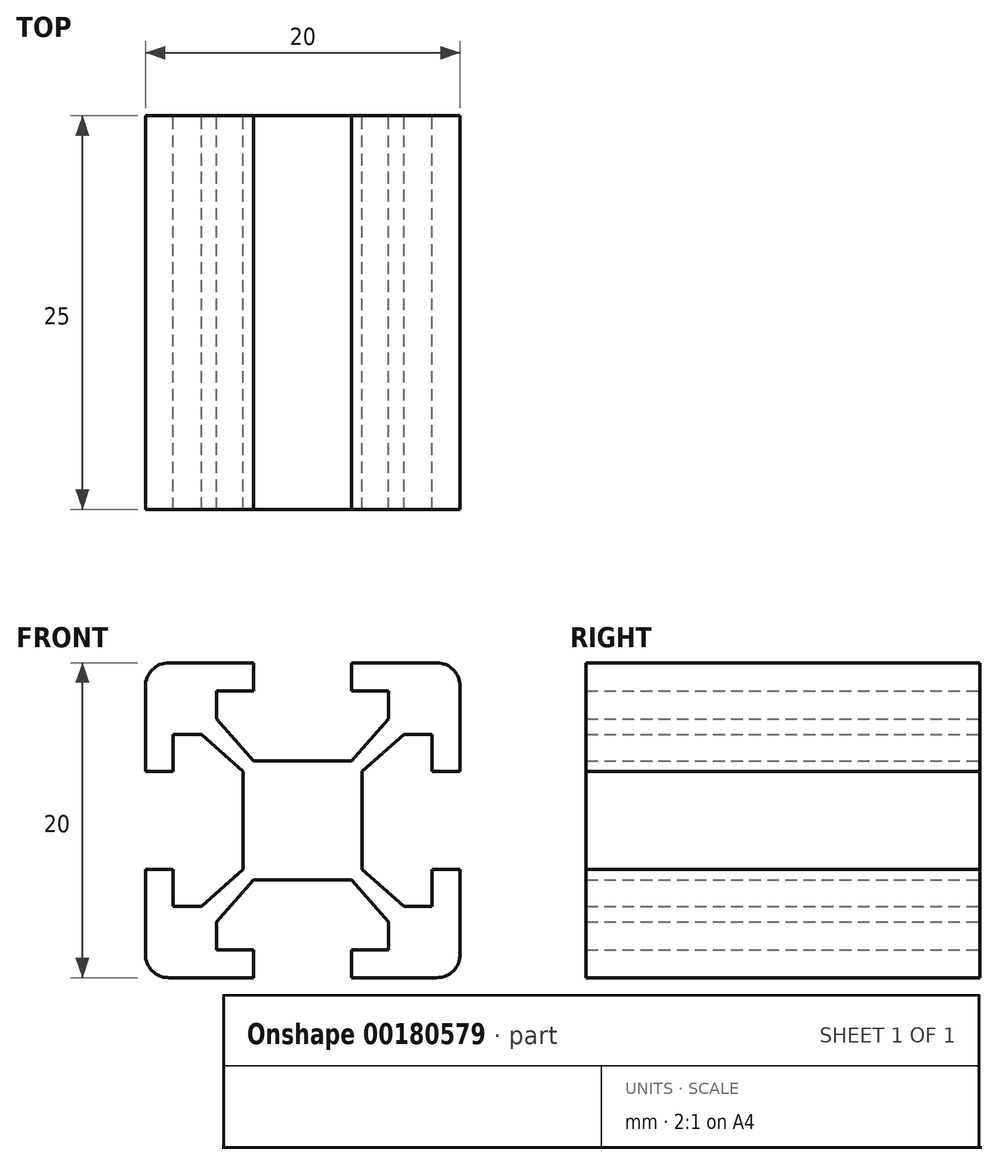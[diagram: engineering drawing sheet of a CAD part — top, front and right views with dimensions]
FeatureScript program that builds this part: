
annotation { "Feature Type Name" : "Feature", "Feature Type Description" : "" }
export const myFeature = defineFeature(function(context is Context, id is Id, definition is map)
    precondition{}
    {
        {
            var Q0;
            Q0=qCreatedBy(makeId("Front.planeOp"),FACE);
            var sketch = newSketch(context, id + "F0", { "sketchPlane" : qUnion([Q0])});
            skLineSegment(sketch, "E0.bottom", {"start": v(10, 10) * mm, "end": v(-10, 10) * mm});
            skLineSegment(sketch, "E0.top", {"start": v(10, -10) * mm, "end": v(-10, -10) * mm});
            skLineSegment(sketch, "E0.left", {"start": v(10, 10) * mm, "end": v(10, -10) * mm});
            skLineSegment(sketch, "E0.right", {"start": v(-10, 10) * mm, "end": v(-10, -10) * mm});
            skPoint(sketch, "E0.middle", {"position": v(0, 0) * mm});
            skLineSegment(sketch, "E1", {"start": v(3.11, 10) * mm, "end": v(3.11, 8.22) * mm});
            skLineSegment(sketch, "E2", {"start": v(3.11, 8.22) * mm, "end": v(5.46, 8.22) * mm});
            skLineSegment(sketch, "E3", {"start": v(5.46, 8.22) * mm, "end": v(5.46, 6.44) * mm});
            skLineSegment(sketch, "E4", {"start": v(5.46, 6.44) * mm, "end": v(3.11, 3.78) * mm});
            skLineSegment(sketch, "E5", {"start": v(3.11, 3.78) * mm, "end": v(0, 3.78) * mm});
            skLineSegment(sketch, "E6.MirrorCS", {"start": v(-3.11, 3.78) * mm, "end": v(0, 3.78) * mm});
            skLineSegment(sketch, "E7.MirrorCS", {"start": v(-5.46, 6.44) * mm, "end": v(-3.11, 3.78) * mm});
            skLineSegment(sketch, "E8.MirrorCS", {"start": v(-3.11, 10) * mm, "end": v(-3.11, 8.22) * mm});
            skLineSegment(sketch, "E9.MirrorCS", {"start": v(-5.46, 8.22) * mm, "end": v(-5.46, 6.44) * mm});
            skLineSegment(sketch, "E10.MirrorCS", {"start": v(-3.11, 8.22) * mm, "end": v(-5.46, 8.22) * mm});
            skLineSegment(sketch, "E11.1.0", {"start": v(-10, 3.11) * mm, "end": v(-8.22, 3.11) * mm});
            skLineSegment(sketch, "E11.1.1", {"start": v(-8.22, 3.11) * mm, "end": v(-8.22, 5.46) * mm});
            skLineSegment(sketch, "E11.1.2", {"start": v(-8.22, 5.46) * mm, "end": v(-6.44, 5.46) * mm});
            skLineSegment(sketch, "E11.1.3", {"start": v(-6.44, 5.46) * mm, "end": v(-3.78, 3.11) * mm});
            skLineSegment(sketch, "E11.1.4", {"start": v(-3.78, 3.11) * mm, "end": v(-3.78, 0) * mm});
            skLineSegment(sketch, "E11.1.5", {"start": v(-3.78, -3.11) * mm, "end": v(-3.78, 0) * mm});
            skLineSegment(sketch, "E11.1.6", {"start": v(-6.44, -5.46) * mm, "end": v(-3.78, -3.11) * mm});
            skLineSegment(sketch, "E11.1.7", {"start": v(-10, -3.11) * mm, "end": v(-8.22, -3.11) * mm});
            skLineSegment(sketch, "E11.1.8", {"start": v(-8.22, -5.46) * mm, "end": v(-6.44, -5.46) * mm});
            skLineSegment(sketch, "E11.1.9", {"start": v(-8.22, -3.11) * mm, "end": v(-8.22, -5.46) * mm});
            skLineSegment(sketch, "E11.2.0", {"start": v(-3.11, -10) * mm, "end": v(-3.11, -8.22) * mm});
            skLineSegment(sketch, "E11.2.1", {"start": v(-3.11, -8.22) * mm, "end": v(-5.46, -8.22) * mm});
            skLineSegment(sketch, "E11.2.2", {"start": v(-5.46, -8.22) * mm, "end": v(-5.46, -6.44) * mm});
            skLineSegment(sketch, "E11.2.3", {"start": v(-5.46, -6.44) * mm, "end": v(-3.11, -3.78) * mm});
            skLineSegment(sketch, "E11.2.4", {"start": v(-3.11, -3.78) * mm, "end": v(0, -3.78) * mm});
            skLineSegment(sketch, "E11.2.5", {"start": v(3.11, -3.78) * mm, "end": v(0, -3.78) * mm});
            skLineSegment(sketch, "E11.2.6", {"start": v(5.46, -6.44) * mm, "end": v(3.11, -3.78) * mm});
            skLineSegment(sketch, "E11.2.7", {"start": v(3.11, -10) * mm, "end": v(3.11, -8.22) * mm});
            skLineSegment(sketch, "E11.2.8", {"start": v(5.46, -8.22) * mm, "end": v(5.46, -6.44) * mm});
            skLineSegment(sketch, "E11.2.9", {"start": v(3.11, -8.22) * mm, "end": v(5.46, -8.22) * mm});
            skLineSegment(sketch, "E11.3.0", {"start": v(10, -3.11) * mm, "end": v(8.22, -3.11) * mm});
            skLineSegment(sketch, "E11.3.1", {"start": v(8.22, -3.11) * mm, "end": v(8.22, -5.46) * mm});
            skLineSegment(sketch, "E11.3.2", {"start": v(8.22, -5.46) * mm, "end": v(6.44, -5.46) * mm});
            skLineSegment(sketch, "E11.3.3", {"start": v(6.44, -5.46) * mm, "end": v(3.78, -3.11) * mm});
            skLineSegment(sketch, "E11.3.4", {"start": v(3.78, -3.11) * mm, "end": v(3.78, 0) * mm});
            skLineSegment(sketch, "E11.3.5", {"start": v(3.78, 3.11) * mm, "end": v(3.78, 0) * mm});
            skLineSegment(sketch, "E11.3.6", {"start": v(6.44, 5.46) * mm, "end": v(3.78, 3.11) * mm});
            skLineSegment(sketch, "E11.3.7", {"start": v(10, 3.11) * mm, "end": v(8.22, 3.11) * mm});
            skLineSegment(sketch, "E11.3.8", {"start": v(8.22, 5.46) * mm, "end": v(6.44, 5.46) * mm});
            skLineSegment(sketch, "E11.3.9", {"start": v(8.22, 3.11) * mm, "end": v(8.22, 5.46) * mm});
            skSolve(sketch);
        }
        {
            var Q0;
            {var subQ12=sQuery(id+"F0.wireOp",EDGE,"E1");Q0=makeQuery(id+"F0.imprint","IMPRINT",FACE,{"disambiguationData":[TD([[makeQuery(id+"F0.imprint","IMPRINT",EDGE,{"derivedFrom":subQ12}),1.0]])]});}
            extrude(context, id + "F1", {"entities" : qUnion([Q0]), "depth" : 25 * mm});
        }
        {
            var Q0;
            Q0=makeQuery(id+"F1.opExtrude","SWEPT_EDGE",EDGE,{"disambiguationData":[OSD([sQuery(id+"F0.wireOp",EDGE,"E0.bottom"),sQuery(id+"F0.wireOp",EDGE,"E0.right")])]});
            var Q1;
            Q1=makeQuery(id+"F1.opExtrude","SWEPT_EDGE",EDGE,{"disambiguationData":[OSD([sQuery(id+"F0.wireOp",EDGE,"E0.bottom"),sQuery(id+"F0.wireOp",EDGE,"E0.left")])]});
            var Q2;
            Q2=makeQuery(id+"F1.opExtrude","SWEPT_EDGE",EDGE,{"disambiguationData":[OSD([sQuery(id+"F0.wireOp",EDGE,"E0.top"),sQuery(id+"F0.wireOp",EDGE,"E0.left")])]});
            var Q3;
            Q3=makeQuery(id+"F1.opExtrude","SWEPT_EDGE",EDGE,{"disambiguationData":[OSD([sQuery(id+"F0.wireOp",EDGE,"E0.top"),sQuery(id+"F0.wireOp",EDGE,"E0.right")])]});
            fillet(context, id + "F2", {"entities" : qUnion([Q0, Q1, Q2, Q3]), "radius" : 1.5 * mm, "tangentPropagation" : true, "allowEdgeOverflow" : false});
        }
    });
